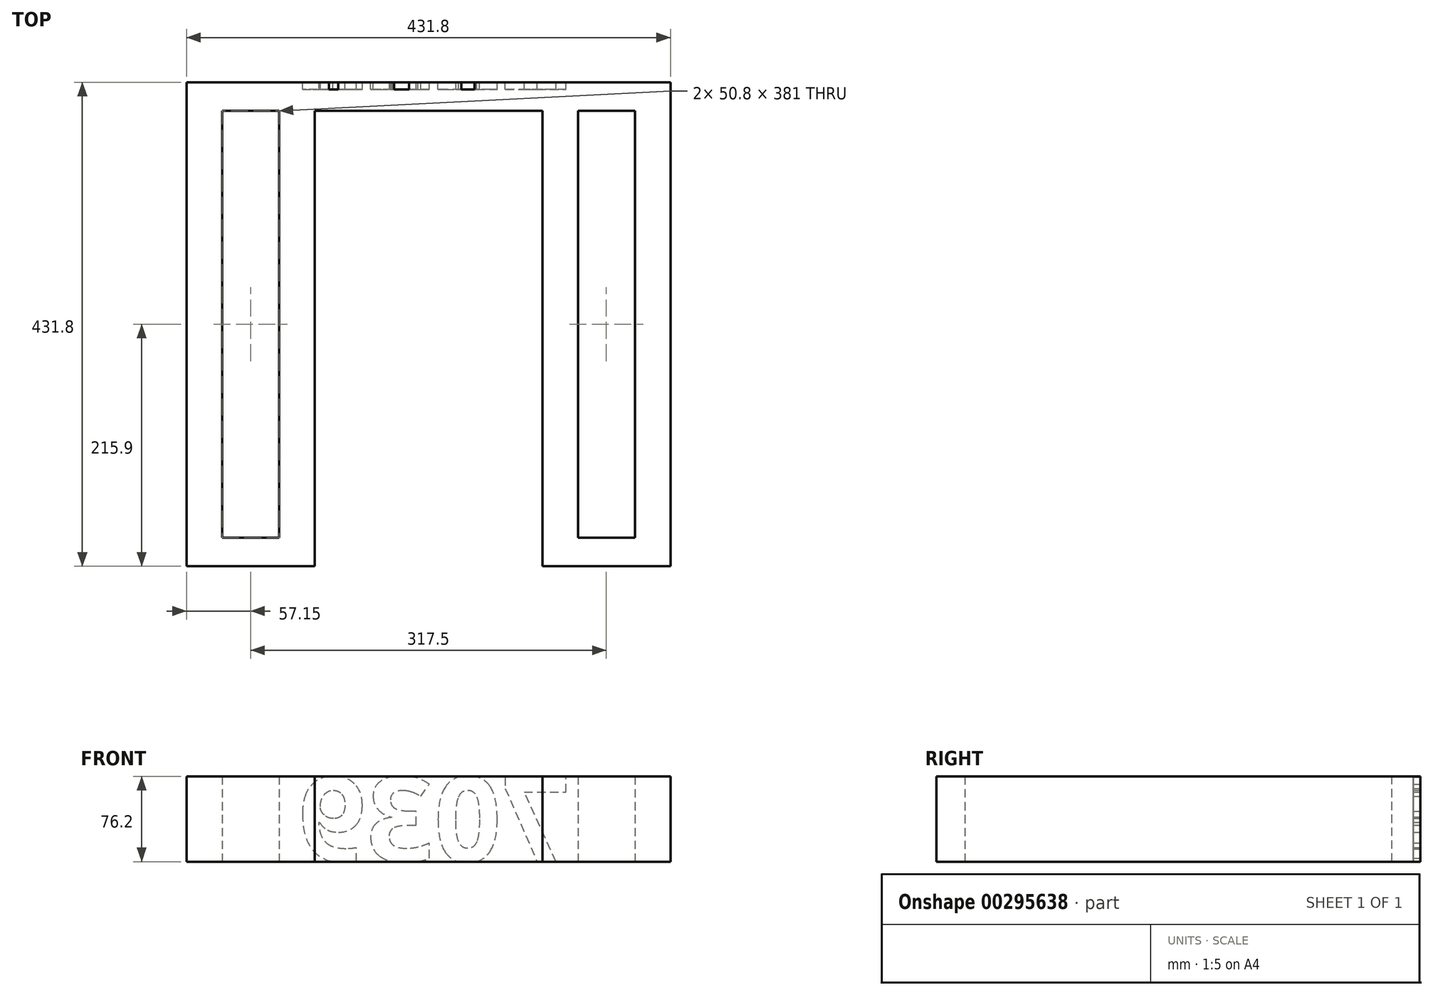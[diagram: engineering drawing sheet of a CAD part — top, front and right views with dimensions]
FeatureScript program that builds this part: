
annotation { "Feature Type Name" : "Feature", "Feature Type Description" : "" }
export const myFeature = defineFeature(function(context is Context, id is Id, definition is map)
    precondition{}
    {
        {
            var Q0;
            Q0=qCreatedBy(makeId("Top.planeOp"),FACE);
            var sketch = newSketch(context, id + "F0", { "sketchPlane" : qUnion([Q0])});
            skLineSegment(sketch, "E0.bottom", {"start": v(-215.9, 215.9) * mm, "end": v(215.9, 215.9) * mm});
            skLineSegment(sketch, "E0.top", {"start": v(-215.9, -215.9) * mm, "end": v(215.9, -215.9) * mm});
            skLineSegment(sketch, "E0.left", {"start": v(-215.9, 215.9) * mm, "end": v(-215.9, -215.9) * mm});
            skLineSegment(sketch, "E0.right", {"start": v(215.9, 215.9) * mm, "end": v(215.9, -215.9) * mm});
            skPoint(sketch, "E0.middle", {"position": v(0, 0) * mm});
            skSolve(sketch);
        }
        {
            var Q0;
            Q0 = qSketchRegion(id + "F0", true);
            extrude(context, id + "F1", {"entities" : qUnion([Q0]), "depth" : 76.2 * mm});
        }
        {
            var Q0;
            Q0=makeQuery(id+"F1.opExtrude","SWEPT_FACE",FACE,{"disambiguationData":[OSD([sQuery(id+"F0.wireOp",EDGE,"E0.top")])]});
            var sketch = newSketch(context, id + "F2", { "sketchPlane" : qUnion([Q0])});
            skLineSegment(sketch, "E1.bottom", {"start": v(-101.6, 0) * mm, "end": v(101.6, 0) * mm});
            skLineSegment(sketch, "E1.top", {"start": v(-101.6, 76.2) * mm, "end": v(101.6, 76.2) * mm});
            skLineSegment(sketch, "E1.left", {"start": v(-101.6, 0) * mm, "end": v(-101.6, 76.2) * mm});
            skLineSegment(sketch, "E1.right", {"start": v(101.6, 0) * mm, "end": v(101.6, 76.2) * mm});
            skPoint(sketch, "E1.middle", {"position": v(0, 38.1) * mm});
            skPoint(sketch, "E1.middle.positionSnap0", {"position": v(0, 0) * mm});
            skPoint(sketch, "E1.centerSnap0", {"position": v(0, 0) * mm});
            skSolve(sketch);
        }
        {
            var Q0;
            Q0=makeQuery(id+"F2.imprint","IMPRINT",FACE,{"disambiguationData":[TD([[makeQuery(id+"F2.imprint","IMPRINT",EDGE,{"derivedFrom":sQuery(id+"F2.wireOp",EDGE,"E1.bottom")}),1.0]])]});
            extrude(context, id + "F3", {"entities" : qUnion([Q0]), "operationType" : NewBodyOperationType.REMOVE, "oppositeDirection" : true, "depth" : 355.6 * mm});
        }
        {
            var Q0;
            Q0=makeQuery(id+"F1.opExtrude","CAP_FACE",FACE,{"disambiguationData":[OSD([sQuery(id+"F0.wireOp",EDGE,"E0.bottom"),sQuery(id+"F0.wireOp",EDGE,"E0.top"),sQuery(id+"F0.wireOp",EDGE,"E0.left"),sQuery(id+"F0.wireOp",EDGE,"E0.right")])],"isStart":true});
            var sketch = newSketch(context, id + "F4", { "sketchPlane" : qUnion([Q0])});
            skLineSegment(sketch, "E2.bottom", {"start": v(-133.35, 190.5) * mm, "end": v(-184.15, 190.5) * mm});
            skLineSegment(sketch, "E2.top", {"start": v(-133.35, -190.5) * mm, "end": v(-184.15, -190.5) * mm});
            skLineSegment(sketch, "E2.left", {"start": v(-133.35, 190.5) * mm, "end": v(-133.35, -190.5) * mm});
            skLineSegment(sketch, "E2.right", {"start": v(-184.15, 190.5) * mm, "end": v(-184.15, -190.5) * mm});
            skPoint(sketch, "E2.middle", {"position": v(-158.75, 0) * mm});
            skPoint(sketch, "E2.middle.positionSnap0", {"position": v(-158.75, 215.9) * mm});
            skPoint(sketch, "E2.centerSnap0", {"position": v(-158.75, 215.9) * mm});
            skLineSegment(sketch, "E3.bottom", {"start": v(133.35, 190.5) * mm, "end": v(184.15, 190.5) * mm});
            skLineSegment(sketch, "E3.top", {"start": v(133.35, -190.5) * mm, "end": v(184.15, -190.5) * mm});
            skLineSegment(sketch, "E3.left", {"start": v(133.35, 190.5) * mm, "end": v(133.35, -190.5) * mm});
            skLineSegment(sketch, "E3.right", {"start": v(184.15, 190.5) * mm, "end": v(184.15, -190.5) * mm});
            skPoint(sketch, "E3.middle", {"position": v(158.75, 0) * mm});
            skPoint(sketch, "E3.middle.positionSnap0", {"position": v(158.75, 215.9) * mm});
            skPoint(sketch, "E3.centerSnap0", {"position": v(158.75, 215.9) * mm});
            skSolve(sketch);
        }
        {
            var Q0;
            Q0=makeQuery(id+"F4.imprint","IMPRINT",FACE,{"disambiguationData":[TD([[makeQuery(id+"F4.imprint","IMPRINT",EDGE,{"derivedFrom":sQuery(id+"F4.wireOp",EDGE,"E3.bottom")}),-1.0]])]});
            var Q1;
            Q1=makeQuery(id+"F4.imprint","IMPRINT",FACE,{"disambiguationData":[TD([[makeQuery(id+"F4.imprint","IMPRINT",EDGE,{"derivedFrom":sQuery(id+"F4.wireOp",EDGE,"E2.bottom")}),1.0]])]});
            extrude(context, id + "F5", {"entities" : qUnion([Q0, Q1]), "operationType" : NewBodyOperationType.REMOVE, "endBound" : BoundingType.THROUGH_ALL, "oppositeDirection" : true, "depth" : 25.4 * mm});
        }
        {
            var Q0;
            Q0=makeQuery(id+"F1.opExtrude","SWEPT_FACE",FACE,{"disambiguationData":[OSD([sQuery(id+"F0.wireOp",EDGE,"E0.bottom")])]});
            var sketch = newSketch(context, id + "F6", { "sketchPlane" : qUnion([Q0])});
            skText(sketch, "E4", { "text": "7039", "fontName": "OpenSans-Bold.ttf"});
            const initialGuessF6  = {"E4": [-0.1256, 0, 1, 0, 0.0762]};
            skSetInitialGuess(sketch, initialGuessF6);
            skSolve(sketch);
        }
        {
            var Q0;
            {var subQ10=sQuery(id+"F6.wireOp",EDGE,"E4.sketch_text.stroke-50");Q0=makeQuery(id+"F6.imprint","IMPRINT",FACE,{"disambiguationData":[TD([[makeQuery(id+"F6.imprint","IMPRINT",EDGE,{"derivedFrom":subQ10}),-1.0]])]});}
            var Q1;
            {var subQ8=sQuery(id+"F6.wireOp",EDGE,"E4.sketch_text.stroke-7");Q1=makeQuery(id+"F6.imprint","IMPRINT",FACE,{"disambiguationData":[TD([[makeQuery(id+"F6.imprint","IMPRINT",EDGE,{"derivedFrom":subQ8}),-1.0]])]});}
            var Q2;
            Q2=makeQuery(id+"F6.imprint","IMPRINT",FACE,{"disambiguationData":[TD([[makeQuery(id+"F6.imprint","IMPRINT",EDGE,{"derivedFrom":sQuery(id+"F6.wireOp",EDGE,"E4.sketch_text.stroke-0")}),-1.0]])]});
            var Q3;
            Q3=makeQuery(id+"F6.imprint","IMPRINT",FACE,{"disambiguationData":[TD([[makeQuery(id+"F6.imprint","IMPRINT",EDGE,{"derivedFrom":sQuery(id+"F6.wireOp",EDGE,"E4.sketch_text.stroke-23")}),-1.0]])]});
            extrude(context, id + "F7", {"entities" : qUnion([Q0, Q1, Q2, Q3]), "operationType" : NewBodyOperationType.REMOVE, "oppositeDirection" : true, "depth" : 6.35 * mm});
        }
        {
            var Q0;
            Q0=makeQuery(id+"F1.opExtrude","CAP_FACE",FACE,{"disambiguationData":[OSD([sQuery(id+"F0.wireOp",EDGE,"E0.bottom"),sQuery(id+"F0.wireOp",EDGE,"E0.top"),sQuery(id+"F0.wireOp",EDGE,"E0.left"),sQuery(id+"F0.wireOp",EDGE,"E0.right")])],"isStart":false});
            var sketch = newSketch(context, id + "F8", { "sketchPlane" : qUnion([Q0])});
            skLineSegment(sketch, "E5.bottom", {"start": v(-101.6, 139.7) * mm, "end": v(101.6, 139.7) * mm});
            skLineSegment(sketch, "E5.top", {"start": v(-101.6, 190.5) * mm, "end": v(101.6, 190.5) * mm});
            skLineSegment(sketch, "E5.left", {"start": v(-101.6, 139.7) * mm, "end": v(-101.6, 190.5) * mm});
            skLineSegment(sketch, "E5.right", {"start": v(101.6, 139.7) * mm, "end": v(101.6, 190.5) * mm});
            skSolve(sketch);
        }
        {
            var Q0;
            Q0 = qSketchRegion(id + "F8", true);
            extrude(context, id + "F9", {"entities" : qUnion([Q0]), "operationType" : NewBodyOperationType.REMOVE, "endBound" : BoundingType.THROUGH_ALL, "oppositeDirection" : true, "depth" : 25.4 * mm});
        }
    });
